# Revit family: PROOX Waste bin 300mm EN
name_source: partatom
category: Furniture
revit_build: Autodesk Revit 2014 (Build: 20130308_1515(x64)
units: mm (PartAtom-declared; Revit-internal decimal feet)

## types (2) — shared parameters
BIM objects producer = www.BIMtelligent.eu
Manufacturer = PROOX Ltd.
URL = http://www.proox.com

## per-type parameters (varying)
| type | Cost | Description | EAN-No. | Material | Model | Specification |
| ONE pure | 298 $ | waste bin 300 mm PROOX ONE pure made from stainless steel | 9120050350038 | PROOX Stainless steel, brushed | PU-200 | Waste bin made out of stainless steel. Surface with fine brushed structure. Cover 1.5 mm thickness. Intended for wall mounting. Perforated design area with 4mm drillings. Integrated bag holder. 37 litres capacity. Includes stainless steel screws and anchors. |
| ONE dark passion | 338 $ | waste bin PROOX ONE dark passion made from aluminum black anodized | 9120050350175 | PROOX Aluminum, black anodised | DP-200 | Waste bin made out from glass pearl blasted and black anodised aluminum. Cover 3 mm thickness. Intended for wall mounting. Perforated design area with 4mm drillings. Integrated bag holder. 37 litres capacity. Includes stainless steel screws and anchors. |

note: column(s) folded — value = type name in every type: Type Comments

## geometry (parser evidence)
native form markers: Sweep x1
no freeform markers — native parametric forms only
